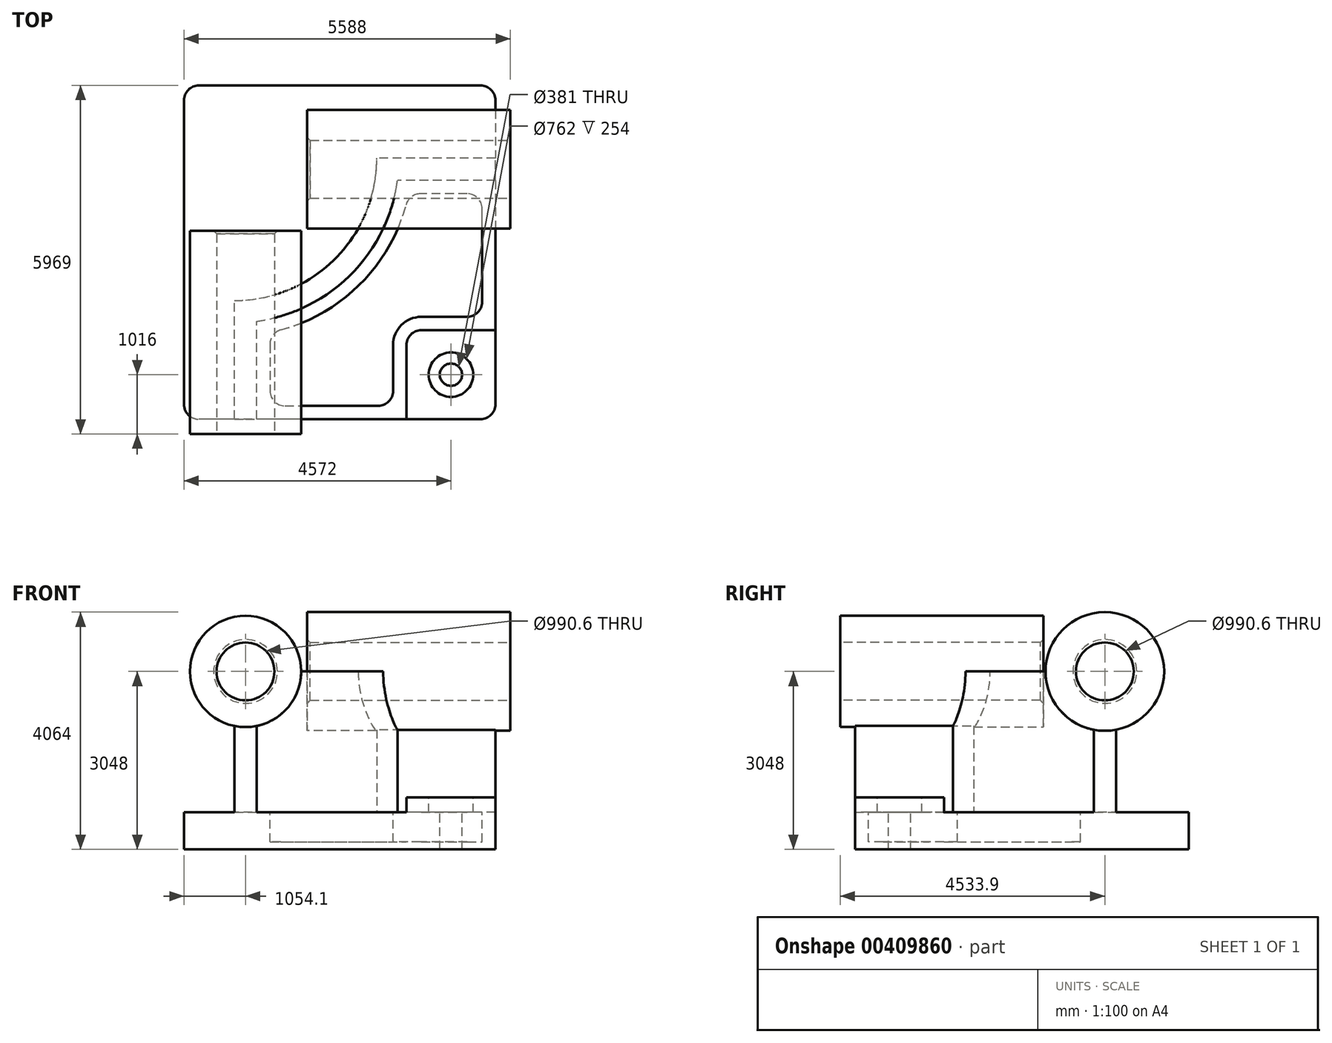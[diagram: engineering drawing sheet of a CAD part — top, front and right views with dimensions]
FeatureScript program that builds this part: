
annotation { "Feature Type Name" : "Feature", "Feature Type Description" : "" }
export const myFeature = defineFeature(function(context is Context, id is Id, definition is map)
    precondition{}
    {
        {
            var Q0;
            Q0=qCreatedBy(makeId("Top.planeOp"),FACE);
            var sketch = newSketch(context, id + "F0", { "sketchPlane" : qUnion([Q0])});
            skLineSegment(sketch, "E0.bottom", {"start": v(2667, 2857.5) * mm, "end": v(-2667, 2857.5) * mm});
            skLineSegment(sketch, "E0.top", {"start": v(2667, -2857.5) * mm, "end": v(-2667, -2857.5) * mm});
            skLineSegment(sketch, "E0.left", {"start": v(2667, 2857.5) * mm, "end": v(2667, -2857.5) * mm});
            skLineSegment(sketch, "E0.right", {"start": v(-2667, 2857.5) * mm, "end": v(-2667, -2857.5) * mm});
            skPoint(sketch, "E0.middle", {"position": v(0, 0) * mm});
            skSolve(sketch);
        }
        {
            var Q0;
            Q0=makeQuery(id+"F0.imprint","IMPRINT",FACE,{"disambiguationData":[TD([[makeQuery(id+"F0.imprint","IMPRINT",EDGE,{"derivedFrom":sQuery(id+"F0.wireOp",EDGE,"E0.bottom")}),1.0]])]});
            extrude(context, id + "F1", {"entities" : qUnion([Q0]), "depth" : 635 * mm});
        }
        {
            var Q0;
            Q0=makeQuery(id+"F1.opExtrude","CAP_FACE",FACE,{"disambiguationData":[OSD([sQuery(id+"F0.wireOp",EDGE,"E0.bottom"),sQuery(id+"F0.wireOp",EDGE,"E0.top"),sQuery(id+"F0.wireOp",EDGE,"E0.left"),sQuery(id+"F0.wireOp",EDGE,"E0.right")])],"isStart":false});
            var sketch = newSketch(context, id + "F2", { "sketchPlane" : qUnion([Q0])});
            skLineSegment(sketch, "E1", {"start": v(-1803.4, -2857.5) * mm, "end": v(-1803.4, -825.5) * mm});
            skLineSegment(sketch, "E2", {"start": v(2667, 1612.9) * mm, "end": v(635, 1612.9) * mm});
            skArc(sketch, "E3", {"start": v(-1803.4, -825.5) * mm, "mid": v(-79.2, -111.3) * mm, "end": v(635, 1612.9) * mm});
            skLineSegment(sketch, "E4", {"start": v(-1803.4, 1612.9) * mm, "end": v(635, 1612.9) * mm, "construction": true});
            skLineSegment(sketch, "E5", {"start": v(-1803.4, 1612.9) * mm, "end": v(-1803.4, -825.5) * mm, "construction": true});
            skLineSegment(sketch, "E6.0", {"start": v(-1422.4, -2857.5) * mm, "end": v(-1422.4, -1180.64) * mm});
            skArc(sketch, "E6.1", {"start": v(-1422.4, -1180.64) * mm, "mid": v(190.22, -380.72) * mm, "end": v(990.14, 1231.9) * mm});
            skLineSegment(sketch, "E6.2", {"start": v(2667, 1231.9) * mm, "end": v(990.14, 1231.9) * mm});
            skLineSegment(sketch, "E7.0", {"start": v(2667, 2857.5) * mm, "end": v(2667, -2857.5) * mm});
            skLineSegment(sketch, "E8.0", {"start": v(2667, -2857.5) * mm, "end": v(-2667, -2857.5) * mm});
            skSolve(sketch);
        }
        {
            var Q0;
            {var subQ2=sQuery(id+"F2.wireOp",EDGE,"E1");Q0=makeQuery(id+"F2.imprint","IMPRINT",FACE,{"disambiguationData":[TD([[makeQuery(id+"F2.imprint","IMPRINT",EDGE,{"derivedFrom":subQ2}),-1.0]])]});}
            extrude(context, id + "F3", {"entities" : qUnion([Q0]), "operationType" : NewBodyOperationType.ADD, "depth" : 2413 * mm});
        }
        {
            var Q0;
            Q0=makeQuery(id+"F3.boolean.opBoolean","MERGE",FACE,{"derivedFrom":[makeQuery(id+"F1.opExtrude","SWEPT_FACE",FACE,{"disambiguationData":[OSD([sQuery(id+"F0.wireOp",EDGE,"E0.top")])]}),makeQuery(id+"F3.opExtrude","SWEPT_FACE",FACE,{"disambiguationData":[OSD([sQuery(id+"F2.wireOp",EDGE,"E8.0")])]})]});
            var sketch = newSketch(context, id + "F4", { "sketchPlane" : qUnion([Q0])});
            skCircle(sketch, "E9", {"center": v(-1612.9, 3048) * mm, "radius": 952.5 * mm});
            skSolve(sketch);
        }
        {
            var Q0;
            Q0 = qSketchRegion(id + "F4", true);
            extrude(context, id + "F5", {"entities" : qUnion([Q0]), "operationType" : NewBodyOperationType.ADD, "depth" : 254 * mm, "hasSecondDirection" : true, "secondDirectionOppositeDirection" : true, "secondDirectionDepth" : 3225.8 * mm});
        }
        {
            var Q0;
            Q0=makeQuery(id+"F3.boolean.opBoolean","MERGE",FACE,{"derivedFrom":[makeQuery(id+"F1.opExtrude","SWEPT_FACE",FACE,{"disambiguationData":[OSD([sQuery(id+"F0.wireOp",EDGE,"E0.left")])]}),makeQuery(id+"F3.opExtrude","SWEPT_FACE",FACE,{"disambiguationData":[OSD([sQuery(id+"F2.wireOp",EDGE,"E7.0")])]})]});
            var sketch = newSketch(context, id + "F6", { "sketchPlane" : qUnion([Q0])});
            skCircle(sketch, "E10", {"center": v(1422.4, 3048) * mm, "radius": 1016 * mm});
            skSolve(sketch);
        }
        {
            var Q0;
            Q0 = qSketchRegion(id + "F6", true);
            extrude(context, id + "F7", {"entities" : qUnion([Q0]), "operationType" : NewBodyOperationType.ADD, "depth" : 254 * mm, "hasSecondDirection" : true, "secondDirectionOppositeDirection" : true, "secondDirectionDepth" : 3225.8 * mm});
        }
        {
            var Q0;
            {var subQ0=sQuery(id+"F0.wireOp",EDGE,"E0.left");var subQ1=sQuery(id+"F0.wireOp",EDGE,"E0.top");Q0=makeQuery(id+"F3.boolean.opBoolean","SPLIT",FACE,{"disambiguationData":[TD([makeQuery(id+"F3.opExtrude","SWEPT_FACE",FACE,{"disambiguationData":[OSD([sQuery(id+"F2.wireOp",EDGE,"E6.0")])]})])],"derivedFrom":makeQuery(id+"F1.opExtrude","CAP_FACE",FACE,{"disambiguationData":[OSD([sQuery(id+"F0.wireOp",EDGE,"E0.bottom"),subQ1,subQ0,sQuery(id+"F0.wireOp",EDGE,"E0.right")])],"isStart":false})});}
            var sketch = newSketch(context, id + "F8", { "sketchPlane" : qUnion([Q0])});
            skLineSegment(sketch, "E11.bottom", {"start": v(2667, -2857.5) * mm, "end": v(1143, -2857.5) * mm});
            skLineSegment(sketch, "E11.top", {"start": v(2667, -1333.5) * mm, "end": v(1143, -1333.5) * mm});
            skLineSegment(sketch, "E11.left", {"start": v(2667, -2857.5) * mm, "end": v(2667, -1333.5) * mm});
            skLineSegment(sketch, "E11.right", {"start": v(1143, -2857.5) * mm, "end": v(1143, -1333.5) * mm});
            skSolve(sketch);
        }
        {
            var Q0;
            Q0 = qSketchRegion(id + "F8", true);
            extrude(context, id + "F9", {"entities" : qUnion([Q0]), "operationType" : NewBodyOperationType.ADD, "depth" : 254 * mm});
        }
        {
            var Q0;
            Q0=makeQuery(id+"F9.opExtrude","SWEPT_EDGE",EDGE,{"disambiguationData":[OSD([sQuery(id+"F8.wireOp",EDGE,"E11.top"),sQuery(id+"F8.wireOp",EDGE,"E11.right")])]});
            fillet(context, id + "F10", {"entities" : qUnion([Q0]), "radius" : 254 * mm, "tangentPropagation" : true, "allowEdgeOverflow" : false});
        }
        {
            var Q0;
            {var subQ0=sQuery(id+"F0.wireOp",EDGE,"E0.left");var subQ1=sQuery(id+"F0.wireOp",EDGE,"E0.top");Q0=makeQuery(id+"F3.boolean.opBoolean","SPLIT",FACE,{"disambiguationData":[TD([makeQuery(id+"F3.opExtrude","SWEPT_FACE",FACE,{"disambiguationData":[OSD([sQuery(id+"F2.wireOp",EDGE,"E6.0")])]})])],"derivedFrom":makeQuery(id+"F1.opExtrude","CAP_FACE",FACE,{"disambiguationData":[OSD([sQuery(id+"F0.wireOp",EDGE,"E0.bottom"),subQ1,subQ0,sQuery(id+"F0.wireOp",EDGE,"E0.right")])],"isStart":false})});}
            var sketch = newSketch(context, id + "F11", { "sketchPlane" : qUnion([Q0])});
            skLineSegment(sketch, "E12.0", {"start": v(-1193.8, -1373.52) * mm, "end": v(-1193.8, -2628.9) * mm});
            skArc(sketch, "E12.1", {"start": v(1183.02, 1003.3) * mm, "mid": v(351.86, -542.36) * mm, "end": v(-1193.8, -1373.52) * mm});
            skLineSegment(sketch, "E12.2", {"start": v(-1193.8, -2628.9) * mm, "end": v(914.4, -2628.9) * mm});
            skLineSegment(sketch, "E12.3", {"start": v(2438.4, 1003.3) * mm, "end": v(1183.02, 1003.3) * mm});
            skLineSegment(sketch, "E12.4", {"start": v(914.4, -2628.9) * mm, "end": v(914.4, -1587.5) * mm});
            skArc(sketch, "E12.5", {"start": v(914.4, -1587.5) * mm, "mid": v(1055.75, -1246.25) * mm, "end": v(1397, -1104.9) * mm});
            skLineSegment(sketch, "E12.6", {"start": v(1397, -1104.9) * mm, "end": v(2438.4, -1104.9) * mm});
            skLineSegment(sketch, "E12.7", {"start": v(2438.4, -1104.9) * mm, "end": v(2438.4, 1003.3) * mm});
            skSolve(sketch);
        }
        {
            var Q0;
            Q0 = qSketchRegion(id + "F11", true);
            extrude(context, id + "F12", {"entities" : qUnion([Q0]), "operationType" : NewBodyOperationType.REMOVE, "oppositeDirection" : true, "depth" : 508 * mm});
        }
        {
            var Q0;
            Q0=makeQuery(id+"F9.opExtrude","CAP_FACE",FACE,{"disambiguationData":[OSD([sQuery(id+"F8.wireOp",EDGE,"E11.bottom"),sQuery(id+"F8.wireOp",EDGE,"E11.top"),sQuery(id+"F8.wireOp",EDGE,"E11.left"),sQuery(id+"F8.wireOp",EDGE,"E11.right")])],"isStart":false});
            var sketch = newSketch(context, id + "F13", { "sketchPlane" : qUnion([Q0])});
            skCircle(sketch, "E13", {"center": v(1905, -2095.5) * mm, "radius": 381 * mm});
            skSolve(sketch);
        }
        {
            var Q0;
            Q0=sQuery(id+"F13.wireOp",VERTEX,"E13.center");
            var Q1;
            Q1=makeQuery(id+"F1.opExtrude","SWEPT_BODY",BODY,{"disambiguationData":[OSD([sQuery(id+"F0.wireOp",EDGE,"E0.bottom"),sQuery(id+"F0.wireOp",EDGE,"E0.top"),sQuery(id+"F0.wireOp",EDGE,"E0.left"),sQuery(id+"F0.wireOp",EDGE,"E0.right")])]});
            hole(context, id + "F14", {"style" : HoleStyle.C_BORE, "endStyle" : HoleEndStyle.THROUGH, "holeDiameter" : 381 * mm, "cBoreDiameter" : 762 * mm, "cBoreDepth" : 254 * mm, "isTappedThrough" : true, "tappedDepth" : 12.7 * mm, "tapClearance" : 3, "locations" : qUnion([Q0]), "scope" : qUnion([Q1])});
        }
        {
            var Q0;
            Q0=makeQuery(id+"F12.boolean.opBoolean","COPY",EDGE,{"derivedFrom":makeQuery(id+"F12.opExtrude","SWEPT_EDGE",EDGE,{"disambiguationData":[OSD([sQuery(id+"F11.wireOp",EDGE,"E12.0"),sQuery(id+"F11.wireOp",EDGE,"E12.1")])]})});
            var Q1;
            Q1=makeQuery(id+"F12.boolean.opBoolean","COPY",EDGE,{"derivedFrom":makeQuery(id+"F12.opExtrude","SWEPT_EDGE",EDGE,{"disambiguationData":[OSD([sQuery(id+"F11.wireOp",EDGE,"E12.1"),sQuery(id+"F11.wireOp",EDGE,"E12.3")])]})});
            var Q2;
            Q2=makeQuery(id+"F12.boolean.opBoolean","COPY",EDGE,{"derivedFrom":makeQuery(id+"F12.opExtrude","SWEPT_EDGE",EDGE,{"disambiguationData":[OSD([sQuery(id+"F11.wireOp",EDGE,"E12.3"),sQuery(id+"F11.wireOp",EDGE,"E12.7")])]})});
            var Q3;
            Q3=makeQuery(id+"F12.boolean.opBoolean","COPY",EDGE,{"derivedFrom":makeQuery(id+"F12.opExtrude","SWEPT_EDGE",EDGE,{"disambiguationData":[OSD([sQuery(id+"F11.wireOp",EDGE,"E12.6"),sQuery(id+"F11.wireOp",EDGE,"E12.7")])]})});
            var Q4;
            Q4=makeQuery(id+"F12.boolean.opBoolean","COPY",EDGE,{"derivedFrom":makeQuery(id+"F12.opExtrude","SWEPT_EDGE",EDGE,{"disambiguationData":[OSD([sQuery(id+"F11.wireOp",EDGE,"E12.2"),sQuery(id+"F11.wireOp",EDGE,"E12.4")])]})});
            var Q5;
            Q5=makeQuery(id+"F12.boolean.opBoolean","COPY",EDGE,{"derivedFrom":makeQuery(id+"F12.opExtrude","SWEPT_EDGE",EDGE,{"disambiguationData":[OSD([sQuery(id+"F11.wireOp",EDGE,"E12.0"),sQuery(id+"F11.wireOp",EDGE,"E12.2")])]})});
            fillet(context, id + "F15", {"entities" : qUnion([Q0, Q1, Q2, Q3, Q4, Q5]), "radius" : 254 * mm, "tangentPropagation" : true, "allowEdgeOverflow" : false});
        }
        {
            var Q0;
            Q0=makeQuery(id+"F5.opExtrude","CAP_FACE",FACE,{"disambiguationData":[OSD([sQuery(id+"F4.wireOp",EDGE,"E9")])],"isStart":false});
            var sketch = newSketch(context, id + "F16", { "sketchPlane" : qUnion([Q0])});
            skCircle(sketch, "E14", {"center": v(-1612.9, 3048) * mm, "radius": 495.3 * mm});
            skSolve(sketch);
        }
        {
            var Q0;
            Q0 = qSketchRegion(id + "F16", true);
            extrude(context, id + "F17", {"entities" : qUnion([Q0]), "operationType" : NewBodyOperationType.REMOVE, "endBound" : BoundingType.THROUGH_ALL, "oppositeDirection" : true, "depth" : 1168.4 * mm});
        }
        {
            var Q0;
            Q0=makeQuery(id+"F7.opExtrude","CAP_FACE",FACE,{"disambiguationData":[OSD([sQuery(id+"F6.wireOp",EDGE,"E10")])],"isStart":false});
            var sketch = newSketch(context, id + "F18", { "sketchPlane" : qUnion([Q0])});
            skCircle(sketch, "E15", {"center": v(1422.4, 3048) * mm, "radius": 495.3 * mm});
            skSolve(sketch);
        }
        {
            var Q0;
            Q0 = qSketchRegion(id + "F18", true);
            extrude(context, id + "F19", {"entities" : qUnion([Q0]), "operationType" : NewBodyOperationType.REMOVE, "endBound" : BoundingType.THROUGH_ALL, "oppositeDirection" : true, "depth" : 1981.2 * mm});
        }
        {
            var Q0;
            Q0=makeQuery(id+"F17.boolean.opBoolean","COPY",EDGE,{"derivedFrom":makeQuery(id+"F17.opExtrude","CAP_EDGE",EDGE,{"disambiguationData":[OSD([sQuery(id+"F16.wireOp",EDGE,"E14")])],"isStart":true})});
            var Q1;
            Q1=makeQuery(id+"F19.boolean.opBoolean","COPY",EDGE,{"derivedFrom":makeQuery(id+"F19.opExtrude","CAP_EDGE",EDGE,{"disambiguationData":[OSD([sQuery(id+"F18.wireOp",EDGE,"E15")])],"isStart":true})});
            var Q2;
            Q2=makeQuery(id+"F19.boolean.opBoolean","INTERSECT",EDGE,{"derivedFrom":[makeQuery(id+"F7.opExtrude","CAP_FACE",FACE,{"disambiguationData":[OSD([sQuery(id+"F6.wireOp",EDGE,"E10")])],"isStart":true}),makeQuery(id+"F19.opExtrude","SWEPT_FACE",FACE,{"disambiguationData":[OSD([sQuery(id+"F18.wireOp",EDGE,"E15")])]})]});
            var Q3;
            Q3=makeQuery(id+"F17.boolean.opBoolean","INTERSECT",EDGE,{"derivedFrom":[makeQuery(id+"F5.opExtrude","CAP_FACE",FACE,{"disambiguationData":[OSD([sQuery(id+"F4.wireOp",EDGE,"E9")])],"isStart":true}),makeQuery(id+"F17.opExtrude","SWEPT_FACE",FACE,{"disambiguationData":[OSD([sQuery(id+"F16.wireOp",EDGE,"E14")])]})]});
            chamfer(context, id + "F20", {"entities" : qUnion([Q0, Q1, Q2, Q3]), "width" : 50.8 * mm, "tangentPropagation" : true});
        }
        {
            var Q0;
            Q0=makeQuery(id+"F1.opExtrude","SWEPT_EDGE",EDGE,{"disambiguationData":[OSD([sQuery(id+"F0.wireOp",EDGE,"E0.top"),sQuery(id+"F0.wireOp",EDGE,"E0.right")])]});
            var Q1;
            Q1=makeQuery(id+"F9.boolean.opBoolean","MERGE",EDGE,{"derivedFrom":[makeQuery(id+"F1.opExtrude","SWEPT_EDGE",EDGE,{"disambiguationData":[OSD([sQuery(id+"F0.wireOp",EDGE,"E0.top"),sQuery(id+"F0.wireOp",EDGE,"E0.left")])]}),makeQuery(id+"F9.opExtrude","SWEPT_EDGE",EDGE,{"disambiguationData":[OSD([sQuery(id+"F8.wireOp",EDGE,"E11.bottom"),sQuery(id+"F8.wireOp",EDGE,"E11.left")])]})]});
            var Q2;
            Q2=makeQuery(id+"F1.opExtrude","SWEPT_EDGE",EDGE,{"disambiguationData":[OSD([sQuery(id+"F0.wireOp",EDGE,"E0.bottom"),sQuery(id+"F0.wireOp",EDGE,"E0.left")])]});
            var Q3;
            Q3=makeQuery(id+"F1.opExtrude","SWEPT_EDGE",EDGE,{"disambiguationData":[OSD([sQuery(id+"F0.wireOp",EDGE,"E0.bottom"),sQuery(id+"F0.wireOp",EDGE,"E0.right")])]});
            fillet(context, id + "F21", {"entities" : qUnion([Q0, Q1, Q2, Q3]), "radius" : 254 * mm, "tangentPropagation" : true, "allowEdgeOverflow" : false});
        }
    });
